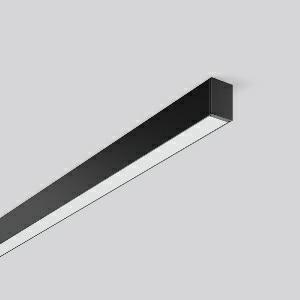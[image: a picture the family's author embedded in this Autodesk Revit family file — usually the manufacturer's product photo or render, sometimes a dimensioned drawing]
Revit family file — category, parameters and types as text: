
# Revit family: less_is_more_27_312200_003_6648
name_source: partatom
category: Lighting Fixtures
units: mm (PartAtom-declared; Revit-internal decimal feet)

## family parameters
Cut with Voids When Loaded = No
Host = Face
Light Source = No
Part Type = Normal
Room Calculation Point = No
Round Connector Dimension = Use Diameter
Shared = No

## types (1)
- LESS IS MORE 27 (1 x LED Modul 830, 2400 lm, 3000)
    Apparent Load = 43 VA
    CIE Flux Codes = 48 79 96 100 100
    Color Rendering = 80
    Color Temperature = 3000
    Default Elevation = 1800 mm
    Description = Series: LESS IS MORE 27
Ceiling and wall luminaire with slim design. Housing: extruded aluminium profile, powder-coated. End cap aluminium powder-coated. Diffuser made of non-yellowing plastic (PMMA), opal. Suitable for Ceiling mounting, Wall (surface). External driver with connecting cable. 
Colour: deep black, matt (RAL 9005)
Length: 1512 mm
Width: 28 mm
Height: 38 mm
Lamp: LED
Socket: without socket
Colour temperature: 3000K
Colour rendering index (CRI): 82
System power: 43 W
Rated luminous flux: 2400 lm
Luminous efficiency: 56 lm/W
Control gear: Regulated power supply
Protection class: II
Type of protection: IP 20
    Height = 38 mm
    Lamp = 1 x LED Modul 830
    Lamp Light Flux = 2400 lm
    Lamp count = 1
    Length = 1512 mm
    Lifetime = 50000 h
    Luminous efficacy = 56 lm/W
    Manufacturer = RZB
    ModVariant = No
    Model = 312200.003
    Mounting Place = Ceiling, Wall
    Mounting Type = Surface mounted
    Number of Poles = 1
    OnlyDefault = Yes
    Power Factor = 1
    Product Name = LESS IS MORE 27
    Product group = Surface mounted LED linear luminaires
    ProductGroupID = 307
    Protection Class = Protection class II
    Protection Degree = IP 20
    RLX_Detail_Level = 1
    RLX_Emergency_Light_Flux = 0 lm
    RLX_Emergency_Type = 0
    RLX_Emergency_Type_DB = No
    RlxData = <blob elided: 28705 chars, md5=373c86ce>
    Socket = socket
    Standby Power = 0 W
    System Light Flux = 2400 lm
    System Power = 43 W
    Type Comments = Product without accessories
    Type Image = 312196.003.jpg
    URL = http://relux.com
    VarID = ---
    Voltage = 230 V
    Voltage Range = 220-240 V
    Weight = 0.00 kg
    Width = 28 mm

## geometry (parser evidence)
native form markers: Blend x4, Sweep x12
no freeform markers — native parametric forms only
